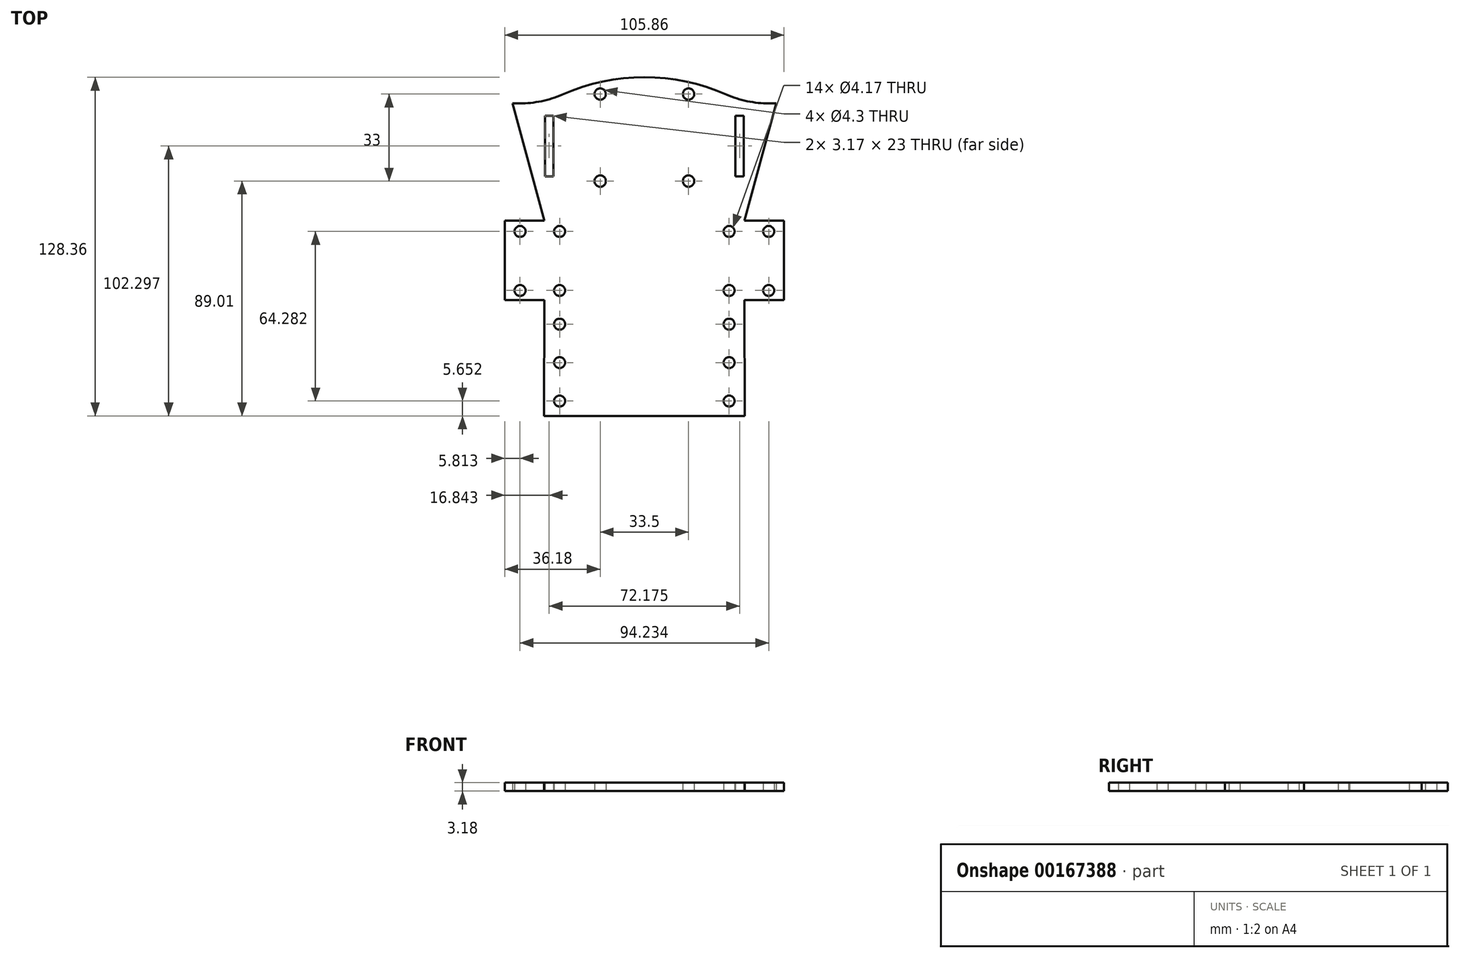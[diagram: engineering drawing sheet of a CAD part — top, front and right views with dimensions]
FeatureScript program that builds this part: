
annotation { "Feature Type Name" : "Feature", "Feature Type Description" : "" }
export const myFeature = defineFeature(function(context is Context, id is Id, definition is map)
    precondition{}
    {
        {
            var Q0;
            Q0=qCreatedBy(makeId("Top.planeOp"),FACE);
            var sketch = newSketch(context, id + "F0", { "sketchPlane" : qUnion([Q0])});
            skLineSegment(sketch, "E0", {"start": v(0, -41.96) * mm, "end": v(38, -41.96) * mm});
            skLineSegment(sketch, "E1.MirrorCS", {"start": v(0, -41.96) * mm, "end": v(-38, -41.96) * mm});
            skArc(sketch, "E2", {"start": v(31.15, 79.85) * mm, "mid": v(0, 86.4) * mm, "end": v(-31.15, 79.85) * mm});
            skCircle(sketch, "E3", {"center": v(-16.75, 80.05) * mm, "radius": 2.15 * mm});
            skCircle(sketch, "E4.MirrorC", {"center": v(16.75, 80.05) * mm, "radius": 2.15 * mm});
            skCircle(sketch, "E5", {"center": v(-16.75, 47.05) * mm, "radius": 2.15 * mm});
            skCircle(sketch, "E6.MirrorC", {"center": v(16.75, 47.05) * mm, "radius": 2.15 * mm});
            skLineSegment(sketch, "E7", {"start": v(38, -41.96) * mm, "end": v(37.94, 2) * mm});
            skLineSegment(sketch, "E8", {"start": v(-38, -41.96) * mm, "end": v(-37.94, 2) * mm});
            skLineSegment(sketch, "E9.bottom", {"start": v(-37.93, 32) * mm, "end": v(-52.93, 32) * mm});
            skLineSegment(sketch, "E9.top", {"start": v(-37.93, 2) * mm, "end": v(-52.93, 2) * mm});
            skLineSegment(sketch, "E9.right", {"start": v(-52.93, 32) * mm, "end": v(-52.93, 2) * mm});
            skLineSegment(sketch, "E10.MirrorCS", {"start": v(37.93, 32) * mm, "end": v(52.93, 32) * mm});
            skLineSegment(sketch, "E11.MirrorCS", {"start": v(52.93, 32) * mm, "end": v(52.93, 2) * mm});
            skLineSegment(sketch, "E12.MirrorCS", {"start": v(37.93, 2) * mm, "end": v(52.93, 2) * mm});
            skLineSegment(sketch, "E13", {"start": v(47.24, 76.48) * mm, "end": v(49.93, 76.48) * mm});
            skLineSegment(sketch, "E14", {"start": v(49.93, 76.48) * mm, "end": v(37.93, 32) * mm});
            skLineSegment(sketch, "E15.MirrorCS", {"start": v(-47.24, 76.48) * mm, "end": v(-49.93, 76.48) * mm});
            skLineSegment(sketch, "E16.MirrorCS", {"start": v(-49.93, 76.48) * mm, "end": v(-37.93, 32) * mm});
            skLineSegment(sketch, "E17.bottom", {"start": v(-34.5, 48.84) * mm, "end": v(-37.67, 48.84) * mm});
            skLineSegment(sketch, "E17.top", {"start": v(-34.5, 71.84) * mm, "end": v(-37.67, 71.84) * mm});
            skLineSegment(sketch, "E17.left", {"start": v(-34.5, 48.84) * mm, "end": v(-34.5, 71.84) * mm});
            skLineSegment(sketch, "E17.right", {"start": v(-37.67, 48.84) * mm, "end": v(-37.67, 71.84) * mm});
            skLineSegment(sketch, "E18.MirrorCS", {"start": v(34.5, 48.84) * mm, "end": v(34.5, 71.84) * mm});
            skLineSegment(sketch, "E19.MirrorCS", {"start": v(34.5, 71.84) * mm, "end": v(37.67, 71.84) * mm});
            skLineSegment(sketch, "E20.MirrorCS", {"start": v(37.67, 48.84) * mm, "end": v(37.67, 71.84) * mm});
            skLineSegment(sketch, "E21.MirrorCS", {"start": v(34.5, 48.84) * mm, "end": v(37.67, 48.84) * mm});
            skPoint(sketch, "E22.visualSharp", {"position": v(-37.93, 76.48) * mm});
            skArc(sketch, "E22.filletArc", {"start": v(-47.24, 76.48) * mm, "mid": v(-39.02, 77.33) * mm, "end": v(-31.15, 79.85) * mm});
            skPoint(sketch, "E23.visualSharp", {"position": v(37.93, 76.48) * mm});
            skArc(sketch, "E23.filletArc", {"start": v(31.15, 79.85) * mm, "mid": v(39.02, 77.33) * mm, "end": v(47.24, 76.48) * mm});
            skCircle(sketch, "E24", {"center": v(-47.12, 27.97) * mm, "radius": 2.08 * mm});
            skCircle(sketch, "E25", {"center": v(-32.12, 27.97) * mm, "radius": 2.08 * mm});
            skCircle(sketch, "E26.MirrorC", {"center": v(-47.12, 5.6) * mm, "radius": 2.08 * mm});
            skCircle(sketch, "E27.MirrorC", {"center": v(-32.12, 5.6) * mm, "radius": 2.08 * mm});
            skCircle(sketch, "E28.MirrorC", {"center": v(32.12, 27.97) * mm, "radius": 2.08 * mm});
            skCircle(sketch, "E29.MirrorC", {"center": v(47.12, 27.97) * mm, "radius": 2.08 * mm});
            skCircle(sketch, "E30.MirrorC", {"center": v(47.12, 5.6) * mm, "radius": 2.08 * mm});
            skCircle(sketch, "E31.MirrorC", {"center": v(32.12, 5.6) * mm, "radius": 2.08 * mm});
            skCircle(sketch, "E32", {"center": v(-32.12, -7.17) * mm, "radius": 2.08 * mm});
            skCircle(sketch, "E33", {"center": v(-32.12, -36.3) * mm, "radius": 2.08 * mm});
            skCircle(sketch, "E34", {"center": v(-32.12, -21.74) * mm, "radius": 2.08 * mm});
            skCircle(sketch, "E35.MirrorC", {"center": v(32.12, -21.74) * mm, "radius": 2.08 * mm});
            skCircle(sketch, "E36.MirrorC", {"center": v(32.12, -36.3) * mm, "radius": 2.08 * mm});
            skCircle(sketch, "E37.MirrorC", {"center": v(32.12, -7.17) * mm, "radius": 2.08 * mm});
            skLineSegment(sketch, "E38", {"start": v(47.12, 27.97) * mm, "end": v(47.12, 5.6) * mm});
            skSolve(sketch);
        }
        {
            var Q0;
            Q0 = qSketchRegion(id + "F0", true);
            extrude(context, id + "F1", {"entities" : qUnion([Q0]), "depth" : 3.17 * mm});
        }
    });
